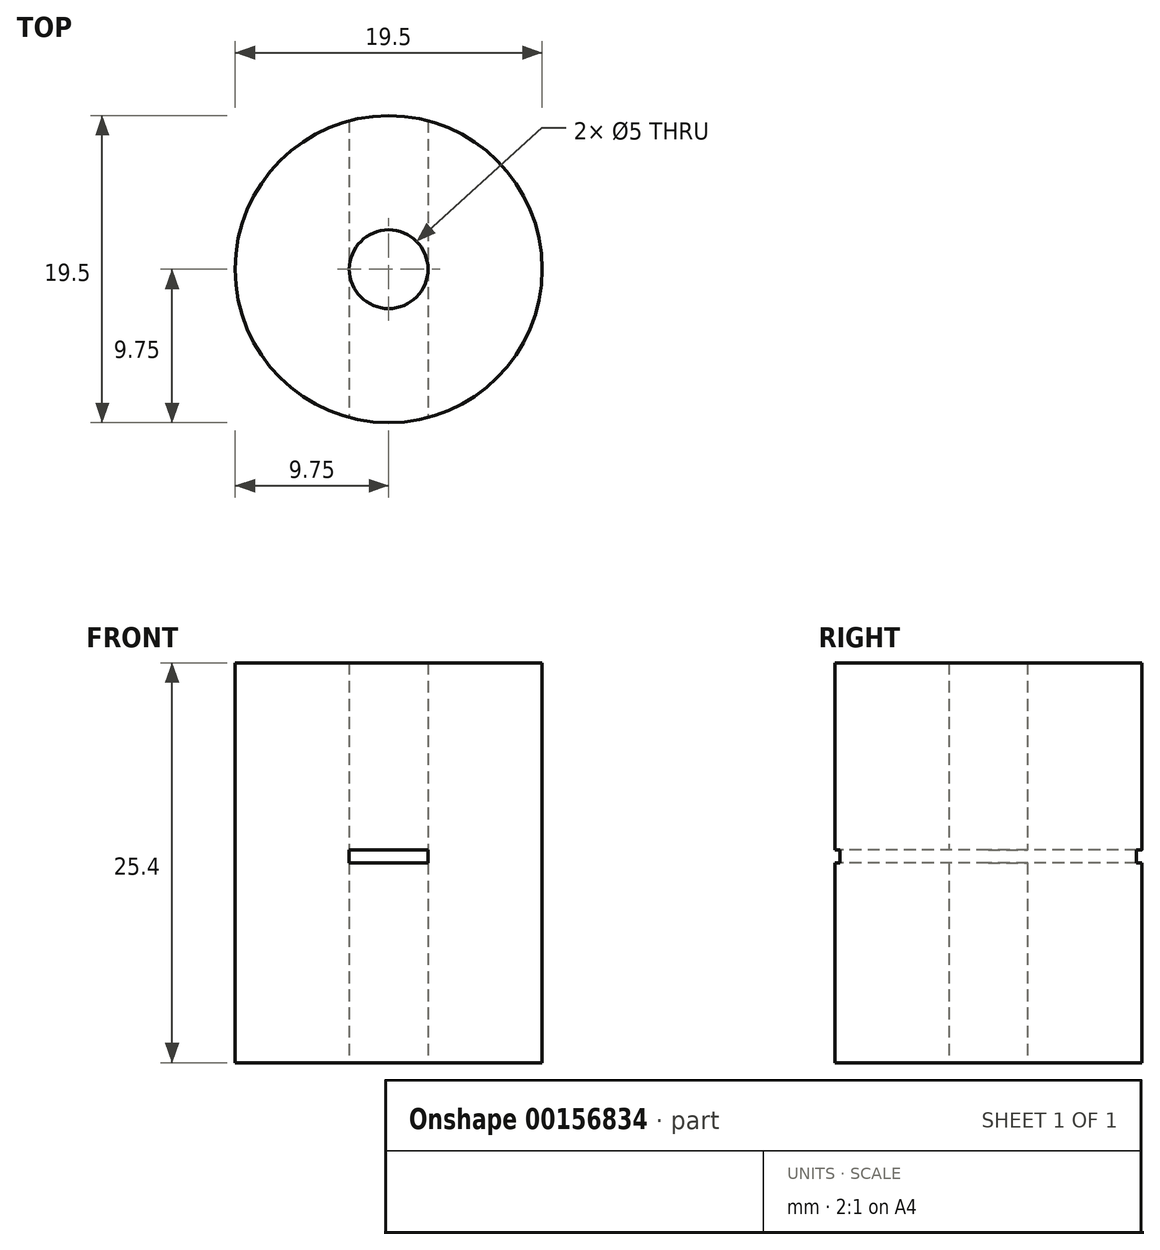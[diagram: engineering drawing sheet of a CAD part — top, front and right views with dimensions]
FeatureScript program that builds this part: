
annotation { "Feature Type Name" : "Feature", "Feature Type Description" : "" }
export const myFeature = defineFeature(function(context is Context, id is Id, definition is map)
    precondition{}
    {
        {
            var Q0;
            Q0=qCreatedBy(makeId("Top.planeOp"),FACE);
            var sketch = newSketch(context, id + "F0", { "sketchPlane" : qUnion([Q0])});
            skCircle(sketch, "E0", {"center": v(0, 0) * mm, "radius": 9.75 * mm});
            skCircle(sketch, "E1", {"center": v(0, 0) * mm, "radius": 2.5 * mm});
            skSolve(sketch);
        }
        {
            var Q0;
            Q0=qSketchRegion(id+"F0",true);
            extrude(context, id + "F1", {"entities" : qUnion([Q0]), "depth" : 25.4 * mm});
        }
        {
            var Q0;
            Q0=qCreatedBy(makeId("Front.planeOp"),FACE);
            var sketch = newSketch(context, id + "F2", { "sketchPlane" : qUnion([Q0])});
            skLineSegment(sketch, "E2.bottom", {"start": v(2.5, 12.7) * mm, "end": v(-2.5, 12.7) * mm});
            skLineSegment(sketch, "E2.top", {"start": v(2.5, 13.5) * mm, "end": v(-2.5, 13.5) * mm});
            skLineSegment(sketch, "E2.left", {"start": v(2.5, 12.7) * mm, "end": v(2.5, 13.5) * mm});
            skLineSegment(sketch, "E2.right", {"start": v(-2.5, 12.7) * mm, "end": v(-2.5, 13.5) * mm});
            skPoint(sketch, "E2.middle", {"position": v(0, 13.1) * mm});
            skSolve(sketch);
        }
        {
            var Q0;
            Q0=qSketchRegion(id+"F2",true);
            extrude(context, id + "F3", {"entities" : qUnion([Q0]), "operationType" : NewBodyOperationType.REMOVE, "endBound" : BoundingType.SYMMETRIC, "oppositeDirection" : true, "depth" : 25.4 * mm});
        }
    });
